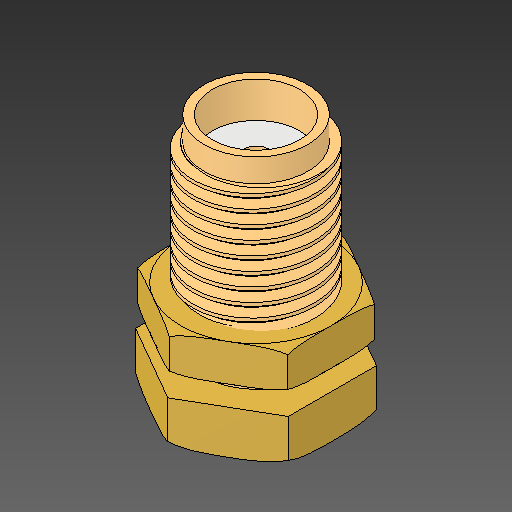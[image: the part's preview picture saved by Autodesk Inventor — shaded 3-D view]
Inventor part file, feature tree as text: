
AUTODESK INVENTOR PART (.ipt)
format: ipt  version: 2018.2 (Build 222227000, 227)  size: 459,264 bytes
history: native  units: mm
features: other x3, chamfer x1
ambient origin geometry x8: Origin, YZ Plane, XZ Plane, XY Plane, X Axis, Y Axis, Z Axis, Center Point
bodies: Body1 (feature_tree), Body2 (feature_tree)
feature tree (4):
  other  "ソリッド1"
  other  "ソリッド2"
  other  "Cut-Revolve2"
  chamfer  "Chamfer1"  [1 undecoded]
note: 1 required parameter value undecoded (feature->parameter linkage not recoverable at this tier; creation-order binding heuristic only, values carry confidence <= 0.55)
